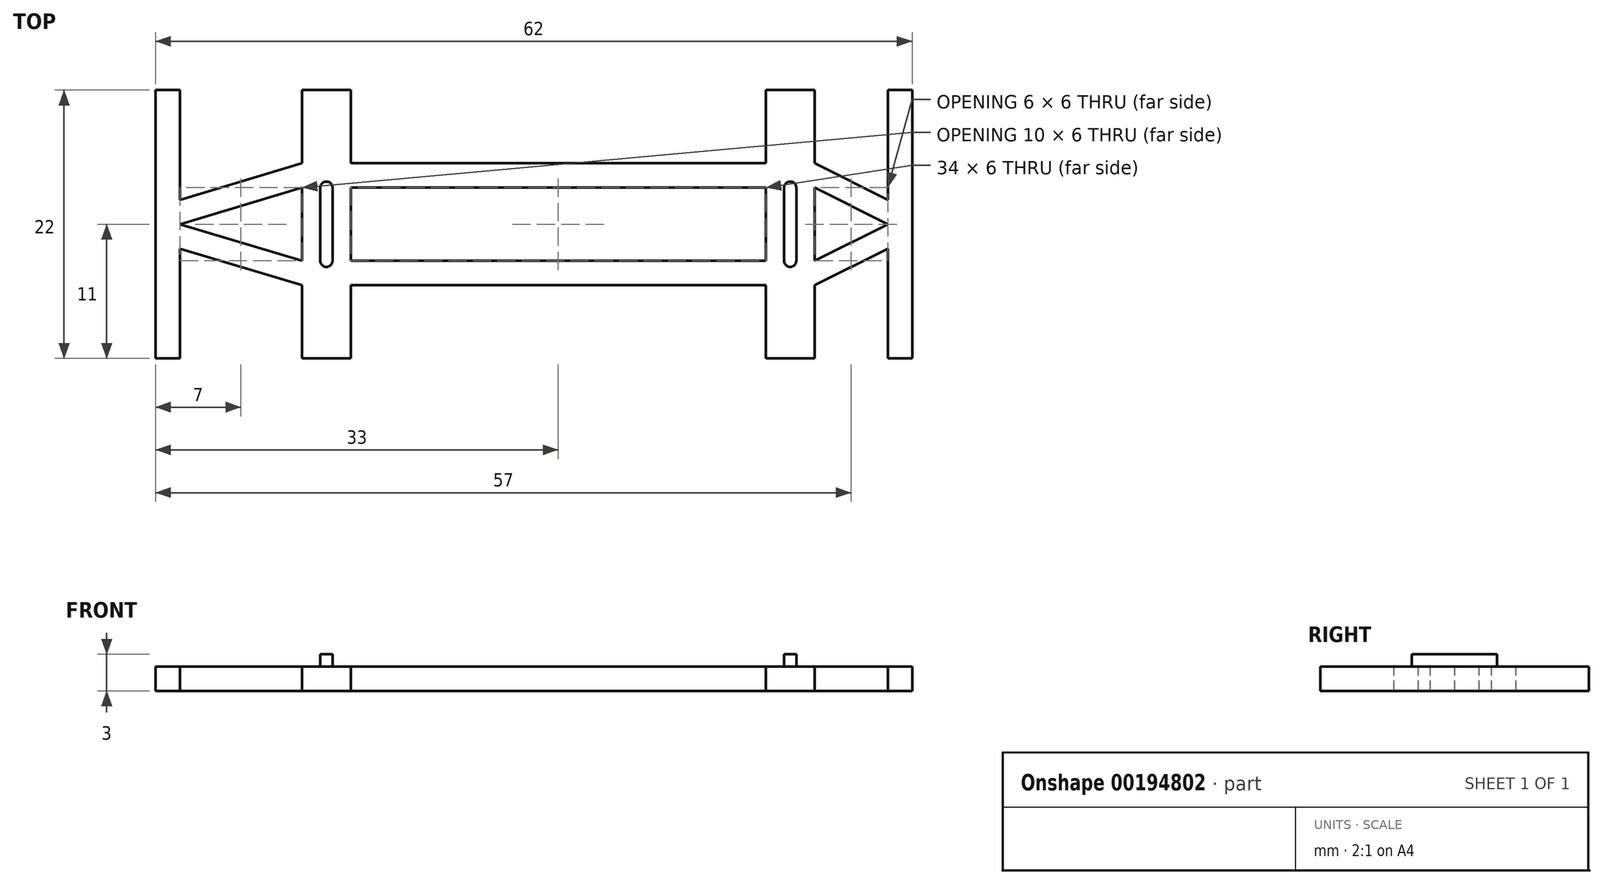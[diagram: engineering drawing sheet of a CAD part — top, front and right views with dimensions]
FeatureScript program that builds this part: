
annotation { "Feature Type Name" : "Feature", "Feature Type Description" : "" }
export const myFeature = defineFeature(function(context is Context, id is Id, definition is map)
    precondition{}
    {
        {
            var Q0;
            Q0=qCreatedBy(makeId("Top.planeOp"),FACE);
            var sketch = newSketch(context, id + "F0", { "sketchPlane" : qUnion([Q0])});
            skLineSegment(sketch, "E0", {"start": v(-24.9, 11) * mm, "end": v(93.99, 11) * mm, "construction": true});
            skLineSegment(sketch, "E1", {"start": v(0, 11) * mm, "end": v(0, 0) * mm});
            skLineSegment(sketch, "E2", {"start": v(0, 0) * mm, "end": v(2, 0) * mm});
            skLineSegment(sketch, "E3", {"start": v(2, 9) * mm, "end": v(2, 0) * mm});
            skLineSegment(sketch, "E4", {"start": v(2, 9) * mm, "end": v(12, 6) * mm});
            skLineSegment(sketch, "E5", {"start": v(12, 6) * mm, "end": v(12, 0) * mm});
            skLineSegment(sketch, "E6", {"start": v(12, 0) * mm, "end": v(16, 0) * mm});
            skLineSegment(sketch, "E7", {"start": v(16, 6) * mm, "end": v(16, 0) * mm});
            skLineSegment(sketch, "E8", {"start": v(16, 6) * mm, "end": v(50, 6) * mm});
            skLineSegment(sketch, "E9", {"start": v(50, 6) * mm, "end": v(50, 0) * mm});
            skLineSegment(sketch, "E10", {"start": v(50, 0) * mm, "end": v(54, 0) * mm});
            skLineSegment(sketch, "E11", {"start": v(54, 0) * mm, "end": v(54, 6) * mm});
            skLineSegment(sketch, "E12", {"start": v(54, 6) * mm, "end": v(60, 9) * mm});
            skLineSegment(sketch, "E13", {"start": v(60, 9) * mm, "end": v(60, 0) * mm});
            skLineSegment(sketch, "E14", {"start": v(60, 0) * mm, "end": v(62, 0) * mm});
            skLineSegment(sketch, "E15", {"start": v(62, 0) * mm, "end": v(62, 11) * mm});
            skLineSegment(sketch, "E16", {"start": v(2, 11) * mm, "end": v(12, 8) * mm});
            skLineSegment(sketch, "E17", {"start": v(16, 11) * mm, "end": v(16, 8) * mm});
            skLineSegment(sketch, "E18", {"start": v(16, 8) * mm, "end": v(50, 8) * mm});
            skLineSegment(sketch, "E19", {"start": v(50, 8) * mm, "end": v(50, 11) * mm});
            skLineSegment(sketch, "E20", {"start": v(60, 11) * mm, "end": v(54, 8) * mm});
            skLineSegment(sketch, "E21", {"start": v(54, 8) * mm, "end": v(54, 11) * mm});
            skLineSegment(sketch, "E22", {"start": v(12, 8) * mm, "end": v(12, 11) * mm});
            skLineSegment(sketch, "E23.MirrorCS", {"start": v(60, 22) * mm, "end": v(62, 22) * mm});
            skLineSegment(sketch, "E24.MirrorCS", {"start": v(12, 14) * mm, "end": v(12, 11) * mm});
            skLineSegment(sketch, "E25.MirrorCS", {"start": v(50, 14) * mm, "end": v(50, 11) * mm});
            skLineSegment(sketch, "E26.MirrorCS", {"start": v(16, 14) * mm, "end": v(50, 14) * mm});
            skLineSegment(sketch, "E27.MirrorCS", {"start": v(60, 13) * mm, "end": v(60, 22) * mm});
            skLineSegment(sketch, "E28.MirrorCS", {"start": v(62, 22) * mm, "end": v(62, 11) * mm});
            skLineSegment(sketch, "E29.MirrorCS", {"start": v(0, 11) * mm, "end": v(0, 22) * mm});
            skLineSegment(sketch, "E30.MirrorCS", {"start": v(0, 22) * mm, "end": v(2, 22) * mm});
            skLineSegment(sketch, "E31.MirrorCS", {"start": v(2, 13) * mm, "end": v(12, 16) * mm});
            skLineSegment(sketch, "E32.MirrorCS", {"start": v(12, 16) * mm, "end": v(12, 22) * mm});
            skLineSegment(sketch, "E33.MirrorCS", {"start": v(54, 16) * mm, "end": v(60, 13) * mm});
            skLineSegment(sketch, "E34.MirrorCS", {"start": v(60, 11) * mm, "end": v(54, 14) * mm});
            skLineSegment(sketch, "E35.MirrorCS", {"start": v(2, 13) * mm, "end": v(2, 22) * mm});
            skLineSegment(sketch, "E36.MirrorCS", {"start": v(54, 14) * mm, "end": v(54, 11) * mm});
            skLineSegment(sketch, "E37.MirrorCS", {"start": v(54, 22) * mm, "end": v(54, 16) * mm});
            skLineSegment(sketch, "E38.MirrorCS", {"start": v(50, 22) * mm, "end": v(54, 22) * mm});
            skLineSegment(sketch, "E39.MirrorCS", {"start": v(50, 16) * mm, "end": v(50, 22) * mm});
            skLineSegment(sketch, "E40.MirrorCS", {"start": v(16, 16) * mm, "end": v(16, 22) * mm});
            skLineSegment(sketch, "E41.MirrorCS", {"start": v(16, 16) * mm, "end": v(50, 16) * mm});
            skLineSegment(sketch, "E42.MirrorCS", {"start": v(16, 11) * mm, "end": v(16, 14) * mm});
            skLineSegment(sketch, "E43.MirrorCS", {"start": v(2, 11) * mm, "end": v(12, 14) * mm});
            skLineSegment(sketch, "E44.MirrorCS", {"start": v(12, 22) * mm, "end": v(16, 22) * mm});
            skSolve(sketch);
        }
        {
            var Q0;
            Q0 = qSketchRegion(id + "F0", true);
            extrude(context, id + "F1", {"entities" : qUnion([Q0]), "depth" : 2 * mm});
        }
        {
            var Q0;
            Q0=makeQuery(id+"F1.opExtrude","CAP_FACE",FACE,{"disambiguationData":[OSD([sQuery(id+"F0.wireOp",EDGE,"E1"),sQuery(id+"F0.wireOp",EDGE,"E2"),sQuery(id+"F0.wireOp",EDGE,"E3"),sQuery(id+"F0.wireOp",EDGE,"E4"),sQuery(id+"F0.wireOp",EDGE,"E5"),sQuery(id+"F0.wireOp",EDGE,"E6"),sQuery(id+"F0.wireOp",EDGE,"E7"),sQuery(id+"F0.wireOp",EDGE,"E8"),sQuery(id+"F0.wireOp",EDGE,"E9"),sQuery(id+"F0.wireOp",EDGE,"E10"),sQuery(id+"F0.wireOp",EDGE,"E11"),sQuery(id+"F0.wireOp",EDGE,"E12"),sQuery(id+"F0.wireOp",EDGE,"E13"),sQuery(id+"F0.wireOp",EDGE,"E14"),sQuery(id+"F0.wireOp",EDGE,"E15"),sQuery(id+"F0.wireOp",EDGE,"E16"),sQuery(id+"F0.wireOp",EDGE,"E17"),sQuery(id+"F0.wireOp",EDGE,"E18"),sQuery(id+"F0.wireOp",EDGE,"E19"),sQuery(id+"F0.wireOp",EDGE,"E20"),sQuery(id+"F0.wireOp",EDGE,"E21"),sQuery(id+"F0.wireOp",EDGE,"E22"),sQuery(id+"F0.wireOp",EDGE,"E23.MirrorCS"),sQuery(id+"F0.wireOp",EDGE,"E24.MirrorCS"),sQuery(id+"F0.wireOp",EDGE,"E25.MirrorCS"),sQuery(id+"F0.wireOp",EDGE,"E26.MirrorCS"),sQuery(id+"F0.wireOp",EDGE,"E27.MirrorCS"),sQuery(id+"F0.wireOp",EDGE,"E28.MirrorCS"),sQuery(id+"F0.wireOp",EDGE,"E29.MirrorCS"),sQuery(id+"F0.wireOp",EDGE,"E30.MirrorCS"),sQuery(id+"F0.wireOp",EDGE,"E31.MirrorCS"),sQuery(id+"F0.wireOp",EDGE,"E32.MirrorCS"),sQuery(id+"F0.wireOp",EDGE,"E33.MirrorCS"),sQuery(id+"F0.wireOp",EDGE,"E34.MirrorCS"),sQuery(id+"F0.wireOp",EDGE,"E35.MirrorCS"),sQuery(id+"F0.wireOp",EDGE,"E36.MirrorCS"),sQuery(id+"F0.wireOp",EDGE,"E37.MirrorCS"),sQuery(id+"F0.wireOp",EDGE,"E38.MirrorCS"),sQuery(id+"F0.wireOp",EDGE,"E39.MirrorCS"),sQuery(id+"F0.wireOp",EDGE,"E40.MirrorCS"),sQuery(id+"F0.wireOp",EDGE,"E41.MirrorCS"),sQuery(id+"F0.wireOp",EDGE,"E42.MirrorCS"),sQuery(id+"F0.wireOp",EDGE,"E43.MirrorCS"),sQuery(id+"F0.wireOp",EDGE,"E44.MirrorCS")])],"isStart":false});
            var sketch = newSketch(context, id + "F2", { "sketchPlane" : qUnion([Q0])});
            skLineSegment(sketch, "E45", {"start": v(14, 14) * mm, "end": v(14, 8) * mm, "construction": true});
            skArc(sketch, "E46", {"start": v(14.5, 14) * mm, "mid": v(14, 14.5) * mm, "end": v(13.5, 14) * mm});
            skArc(sketch, "E47", {"start": v(13.5, 8) * mm, "mid": v(14, 7.5) * mm, "end": v(14.5, 8) * mm});
            skLineSegment(sketch, "E48", {"start": v(13.5, 14) * mm, "end": v(13.5, 8) * mm});
            skLineSegment(sketch, "E49", {"start": v(14.5, 14) * mm, "end": v(14.5, 8) * mm});
            skLineSegment(sketch, "E50", {"start": v(14, 14) * mm, "end": v(16.1, 14) * mm, "construction": true});
            skPoint(sketch, "E51.endSnap0", {"position": v(33, 14) * mm});
            skLineSegment(sketch, "E52", {"start": v(33, 20.8) * mm, "end": v(33, 0) * mm, "construction": true});
            skPoint(sketch, "E52.startSnap0", {"position": v(33, 16) * mm});
            skPoint(sketch, "E52.endSnap0", {"position": v(33, 6) * mm});
            skArc(sketch, "E53.MirrorCS", {"start": v(13.5, 14) * mm, "mid": v(14, 14.5) * mm, "end": v(14.5, 14) * mm});
            skArc(sketch, "E54.MirrorCS", {"start": v(14.5, 8) * mm, "mid": v(14, 7.5) * mm, "end": v(13.5, 8) * mm});
            skLineSegment(sketch, "E55.MirrorCS", {"start": v(14, 14) * mm, "end": v(11.9, 14) * mm, "construction": true});
            skArc(sketch, "E56.MirrorCS", {"start": v(52.5, 14) * mm, "mid": v(52, 14.5) * mm, "end": v(51.5, 14) * mm});
            skArc(sketch, "E57.MirrorCS", {"start": v(51.5, 14) * mm, "mid": v(52, 14.5) * mm, "end": v(52.5, 14) * mm});
            skArc(sketch, "E58.MirrorCS", {"start": v(52.5, 8) * mm, "mid": v(52, 7.5) * mm, "end": v(51.5, 8) * mm});
            skArc(sketch, "E59.MirrorCS", {"start": v(51.5, 8) * mm, "mid": v(52, 7.5) * mm, "end": v(52.5, 8) * mm});
            skLineSegment(sketch, "E60.MirrorCS", {"start": v(52.5, 14) * mm, "end": v(52.5, 8) * mm});
            skLineSegment(sketch, "E61.MirrorCS", {"start": v(51.5, 14) * mm, "end": v(51.5, 8) * mm});
            skLineSegment(sketch, "E62.MirrorCS", {"start": v(52, 14) * mm, "end": v(49.9, 14) * mm, "construction": true});
            skLineSegment(sketch, "E63.MirrorCS", {"start": v(52, 14) * mm, "end": v(54.1, 14) * mm, "construction": true});
            skLineSegment(sketch, "E64.MirrorCS", {"start": v(52, 14) * mm, "end": v(52, 8) * mm, "construction": true});
            skSolve(sketch);
        }
        {
            var Q0;
            Q0 = qSketchRegion(id + "F2", true);
            extrude(context, id + "F3", {"entities" : qUnion([Q0]), "operationType" : NewBodyOperationType.ADD, "depth" : 1 * mm});
        }
    });
